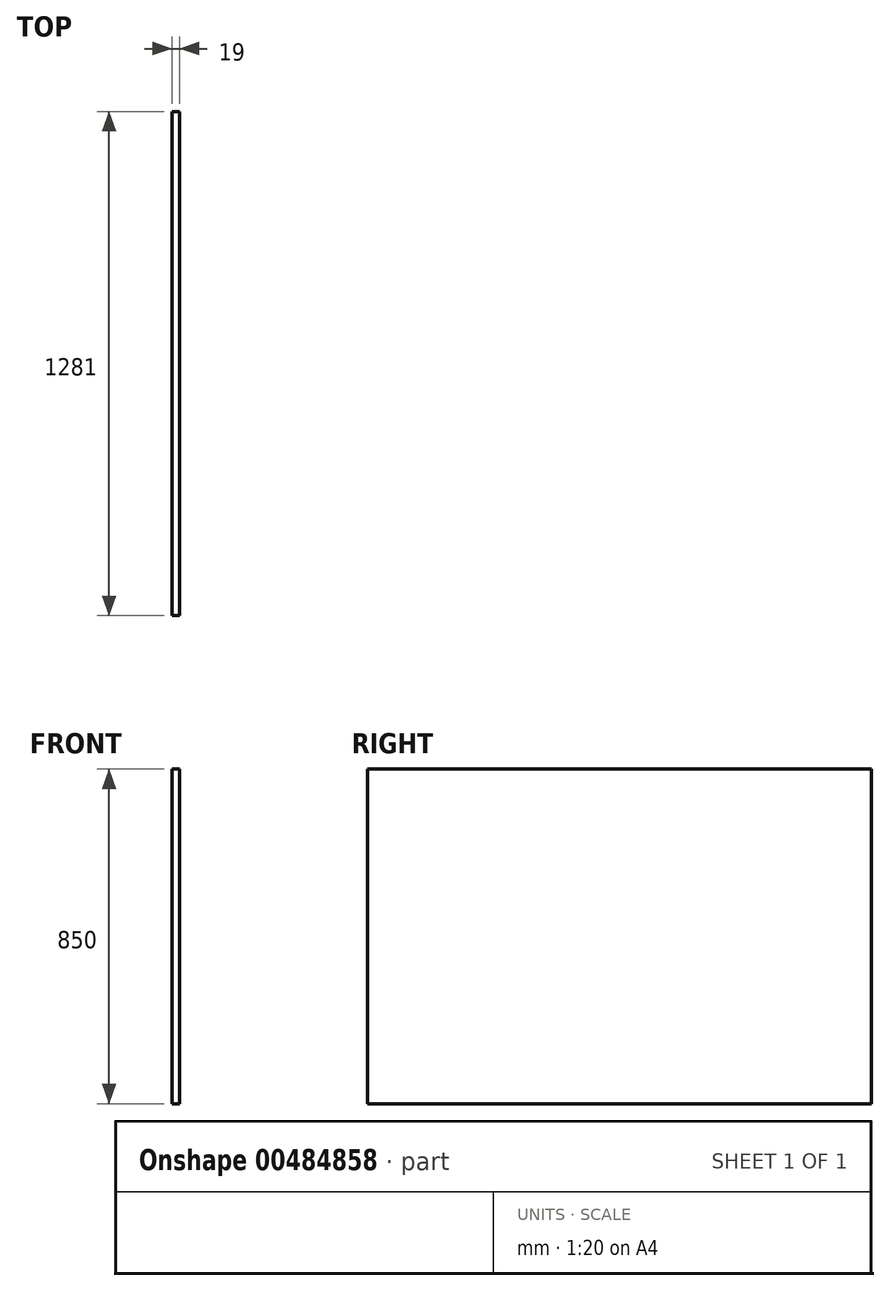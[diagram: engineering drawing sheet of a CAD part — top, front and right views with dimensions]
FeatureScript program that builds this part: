
annotation { "Feature Type Name" : "Feature", "Feature Type Description" : "" }
export const myFeature = defineFeature(function(context is Context, id is Id, definition is map)
    precondition{}
    {
        {
            var Q0;
            Q0=qCreatedBy(makeId("Right.planeOp"),FACE);
            var sketch = newSketch(context, id + "F0", { "sketchPlane" : qUnion([Q0])});
            skLineSegment(sketch, "E0.bottom", {"start": v(-567.23, 547.51) * mm, "end": v(713.77, 547.51) * mm});
            skLineSegment(sketch, "E0.top", {"start": v(-567.23, -302.49) * mm, "end": v(713.77, -302.49) * mm});
            skLineSegment(sketch, "E0.left", {"start": v(-567.23, 547.51) * mm, "end": v(-567.23, -302.49) * mm});
            skLineSegment(sketch, "E0.right", {"start": v(713.77, 547.51) * mm, "end": v(713.77, -302.49) * mm});
            skSolve(sketch);
        }
        {
            var Q0;
            Q0=makeQuery(id+"F0.imprint","IMPRINT",FACE,{"disambiguationData":[TD([[makeQuery(id+"F0.imprint","IMPRINT",EDGE,{"derivedFrom":sQuery(id+"F0.wireOp",EDGE,"E0.bottom")}),-1.0]])]});
            extrude(context, id + "F1", {"entities" : qUnion([Q0]), "depth" : 19 * mm});
        }
    });
